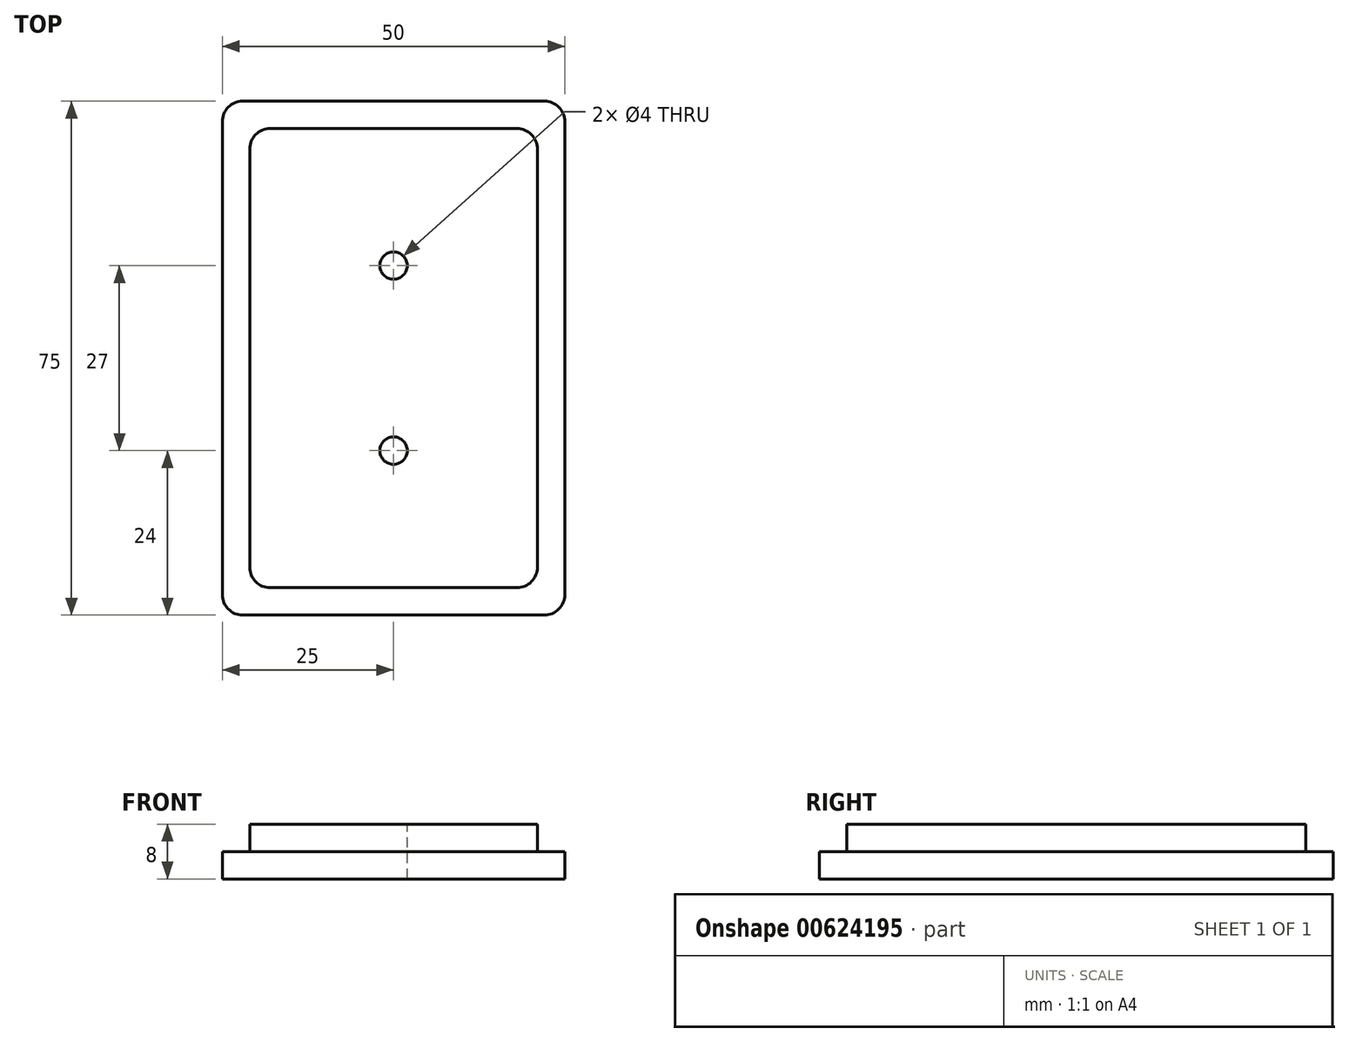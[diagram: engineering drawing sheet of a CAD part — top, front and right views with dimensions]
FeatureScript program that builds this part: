
annotation { "Feature Type Name" : "Feature", "Feature Type Description" : "" }
export const myFeature = defineFeature(function(context is Context, id is Id, definition is map)
    precondition{}
    {
        {
            var Q0;
            Q0=qCreatedBy(makeId("Top.planeOp"),FACE);
            var sketch = newSketch(context, id + "F0", { "sketchPlane" : qUnion([Q0])});
            skLineSegment(sketch, "E0.bottom", {"start": v(0, 0) * mm, "end": v(50, 0) * mm});
            skLineSegment(sketch, "E0.top", {"start": v(0, -75) * mm, "end": v(50, -75) * mm});
            skLineSegment(sketch, "E0.left", {"start": v(0, 0) * mm, "end": v(0, -75) * mm});
            skLineSegment(sketch, "E0.right", {"start": v(50, 0) * mm, "end": v(50, -75) * mm});
            skSolve(sketch);
        }
        {
            var Q0;
            Q0=makeQuery(id+"F0.imprint","IMPRINT",FACE,{"disambiguationData":[TD([[makeQuery(id+"F0.imprint","IMPRINT",EDGE,{"derivedFrom":sQuery(id+"F0.wireOp",EDGE,"E0.bottom")}),-1.0]])]});
            var Q1;
            Q1 = qSketchRegion(id + "F0", true);
            extrude(context, id + "F1", {"entities" : qUnion([Q0, Q1]), "depth" : 4 * mm, "offsetDistance" : 25 * mm});
        }
        {
            var Q0;
            Q0=makeQuery(id+"F1.opExtrude","CAP_FACE",FACE,{"disambiguationData":[OSD([sQuery(id+"F0.wireOp",EDGE,"E0.bottom"),sQuery(id+"F0.wireOp",EDGE,"E0.top"),sQuery(id+"F0.wireOp",EDGE,"E0.left"),sQuery(id+"F0.wireOp",EDGE,"E0.right")])],"isStart":false});
            var sketch = newSketch(context, id + "F2", { "sketchPlane" : qUnion([Q0])});
            skLineSegment(sketch, "E1.bottom", {"start": v(4, -4) * mm, "end": v(46, -4) * mm});
            skLineSegment(sketch, "E1.top", {"start": v(4, -71) * mm, "end": v(46, -71) * mm});
            skLineSegment(sketch, "E1.left", {"start": v(4, -4) * mm, "end": v(4, -71) * mm});
            skLineSegment(sketch, "E1.right", {"start": v(46, -4) * mm, "end": v(46, -71) * mm});
            skSolve(sketch);
        }
        {
            var Q0;
            Q0 = qSketchRegion(id + "F2", true);
            extrude(context, id + "F3", {"entities" : qUnion([Q0]), "operationType" : NewBodyOperationType.ADD, "depth" : 4 * mm, "offsetDistance" : 25 * mm});
        }
        {
            var Q0;
            Q0=makeQuery(id+"F1.opExtrude","SWEPT_EDGE",EDGE,{"disambiguationData":[OSD([sQuery(id+"F0.wireOp",EDGE,"E0.bottom"),sQuery(id+"F0.wireOp",EDGE,"E0.right")])]});
            var Q1;
            Q1=makeQuery(id+"F3.opExtrude","SWEPT_EDGE",EDGE,{"disambiguationData":[OSD([sQuery(id+"F2.wireOp",EDGE,"E1.bottom"),sQuery(id+"F2.wireOp",EDGE,"E1.left")])]});
            var Q2;
            Q2=makeQuery(id+"F1.opExtrude","SWEPT_EDGE",EDGE,{"disambiguationData":[OSD([sQuery(id+"F0.wireOp",EDGE,"E0.bottom"),sQuery(id+"F0.wireOp",EDGE,"E0.left")])]});
            var Q3;
            Q3=makeQuery(id+"F3.opExtrude","SWEPT_EDGE",EDGE,{"disambiguationData":[OSD([sQuery(id+"F2.wireOp",EDGE,"E1.bottom"),sQuery(id+"F2.wireOp",EDGE,"E1.right")])]});
            var Q4;
            Q4=makeQuery(id+"F3.opExtrude","SWEPT_EDGE",EDGE,{"disambiguationData":[OSD([sQuery(id+"F2.wireOp",EDGE,"E1.top"),sQuery(id+"F2.wireOp",EDGE,"E1.right")])]});
            var Q5;
            Q5=makeQuery(id+"F1.opExtrude","SWEPT_EDGE",EDGE,{"disambiguationData":[OSD([sQuery(id+"F0.wireOp",EDGE,"E0.top"),sQuery(id+"F0.wireOp",EDGE,"E0.right")])]});
            var Q6;
            Q6=makeQuery(id+"F3.opExtrude","SWEPT_EDGE",EDGE,{"disambiguationData":[OSD([sQuery(id+"F2.wireOp",EDGE,"E1.top"),sQuery(id+"F2.wireOp",EDGE,"E1.left")])]});
            var Q7;
            Q7=makeQuery(id+"F1.opExtrude","SWEPT_EDGE",EDGE,{"disambiguationData":[OSD([sQuery(id+"F0.wireOp",EDGE,"E0.top"),sQuery(id+"F0.wireOp",EDGE,"E0.left")])]});
            fillet(context, id + "F4", {"entities" : qUnion([Q0, Q1, Q2, Q3, Q4, Q5, Q6, Q7]), "radius" : 3 * mm, "tangentPropagation" : true, "allowEdgeOverflow" : false});
        }
        {
            var Q0;
            Q0=makeQuery(id+"F3.opExtrude","CAP_FACE",FACE,{"disambiguationData":[OSD([sQuery(id+"F2.wireOp",EDGE,"E1.bottom"),sQuery(id+"F2.wireOp",EDGE,"E1.top"),sQuery(id+"F2.wireOp",EDGE,"E1.left"),sQuery(id+"F2.wireOp",EDGE,"E1.right")])],"isStart":false});
            var sketch = newSketch(context, id + "F5", { "sketchPlane" : qUnion([Q0])});
            skCircle(sketch, "E2", {"center": v(25, -51) * mm, "radius": 2 * mm});
            skCircle(sketch, "E3", {"center": v(25, -24) * mm, "radius": 2 * mm});
            skSolve(sketch);
        }
        {
            var Q0;
            Q0 = qSketchRegion(id + "F5", true);
            extrude(context, id + "F6", {"entities" : qUnion([Q0]), "operationType" : NewBodyOperationType.REMOVE, "oppositeDirection" : true, "depth" : 25 * mm, "offsetDistance" : 25 * mm});
        }
    });
